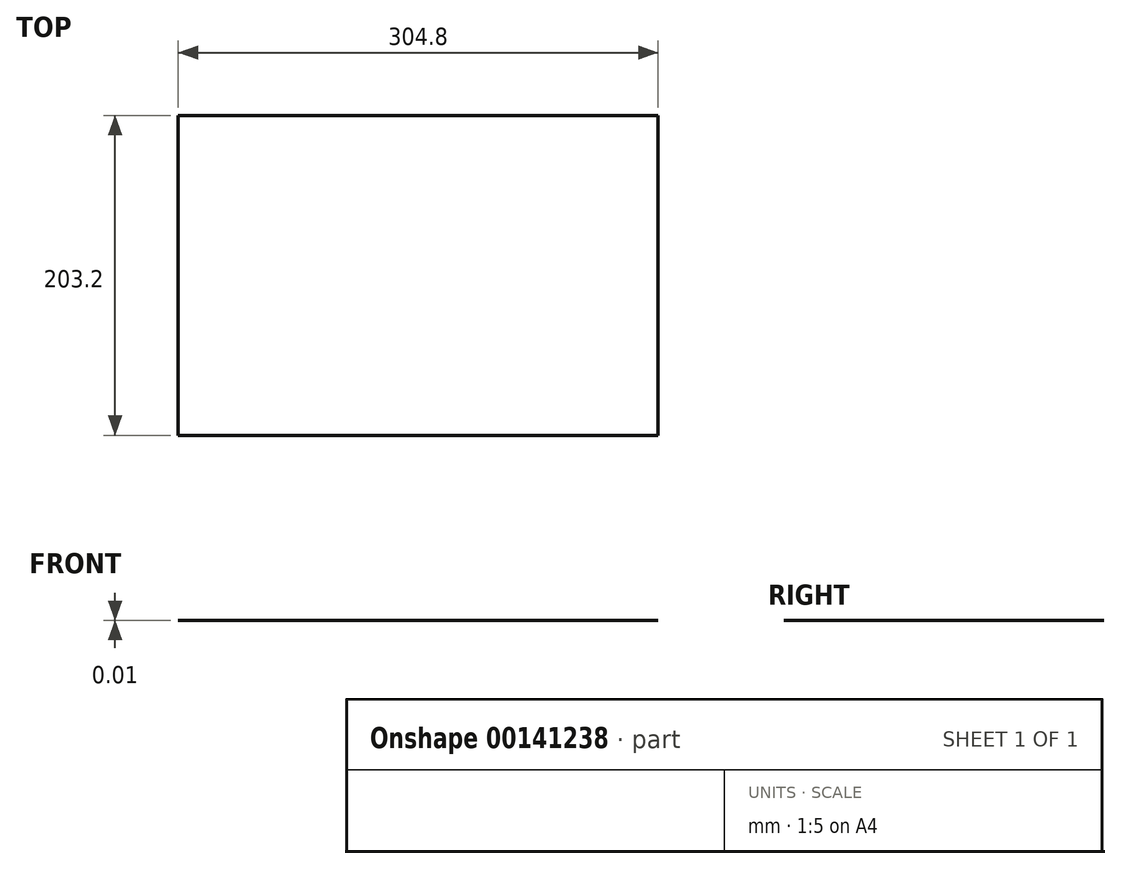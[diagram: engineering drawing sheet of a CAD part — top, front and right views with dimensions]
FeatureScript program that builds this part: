
annotation { "Feature Type Name" : "Feature", "Feature Type Description" : "" }
export const myFeature = defineFeature(function(context is Context, id is Id, definition is map)
    precondition{}
    {
        {
            var Q0;
            Q0=qCreatedBy(makeId("Top.planeOp"),FACE);
            var sketch = newSketch(context, id + "F0", { "sketchPlane" : qUnion([Q0])});
            skLineSegment(sketch, "E0.bottom", {"start": v(152.4, -101.6) * mm, "end": v(-152.4, -101.6) * mm});
            skLineSegment(sketch, "E0.top", {"start": v(152.4, 101.6) * mm, "end": v(-152.4, 101.6) * mm});
            skLineSegment(sketch, "E0.left", {"start": v(152.4, -101.6) * mm, "end": v(152.4, 101.6) * mm});
            skLineSegment(sketch, "E0.right", {"start": v(-152.4, -101.6) * mm, "end": v(-152.4, 101.6) * mm});
            skPoint(sketch, "E0.middle", {"position": v(0, 0) * mm});
            skSolve(sketch);
        }
        {
            var Q0;
            Q0=makeQuery(id+"F0.imprint","IMPRINT",FACE,{"disambiguationData":[TD([[makeQuery(id+"F0.imprint","IMPRINT",EDGE,{"derivedFrom":sQuery(id+"F0.wireOp",EDGE,"E0.bottom")}),-1.0]])]});
            extrude(context, id + "F1", {"entities" : qUnion([Q0]), "depth" : 1 / 101.6 * mm});
        }
    });
